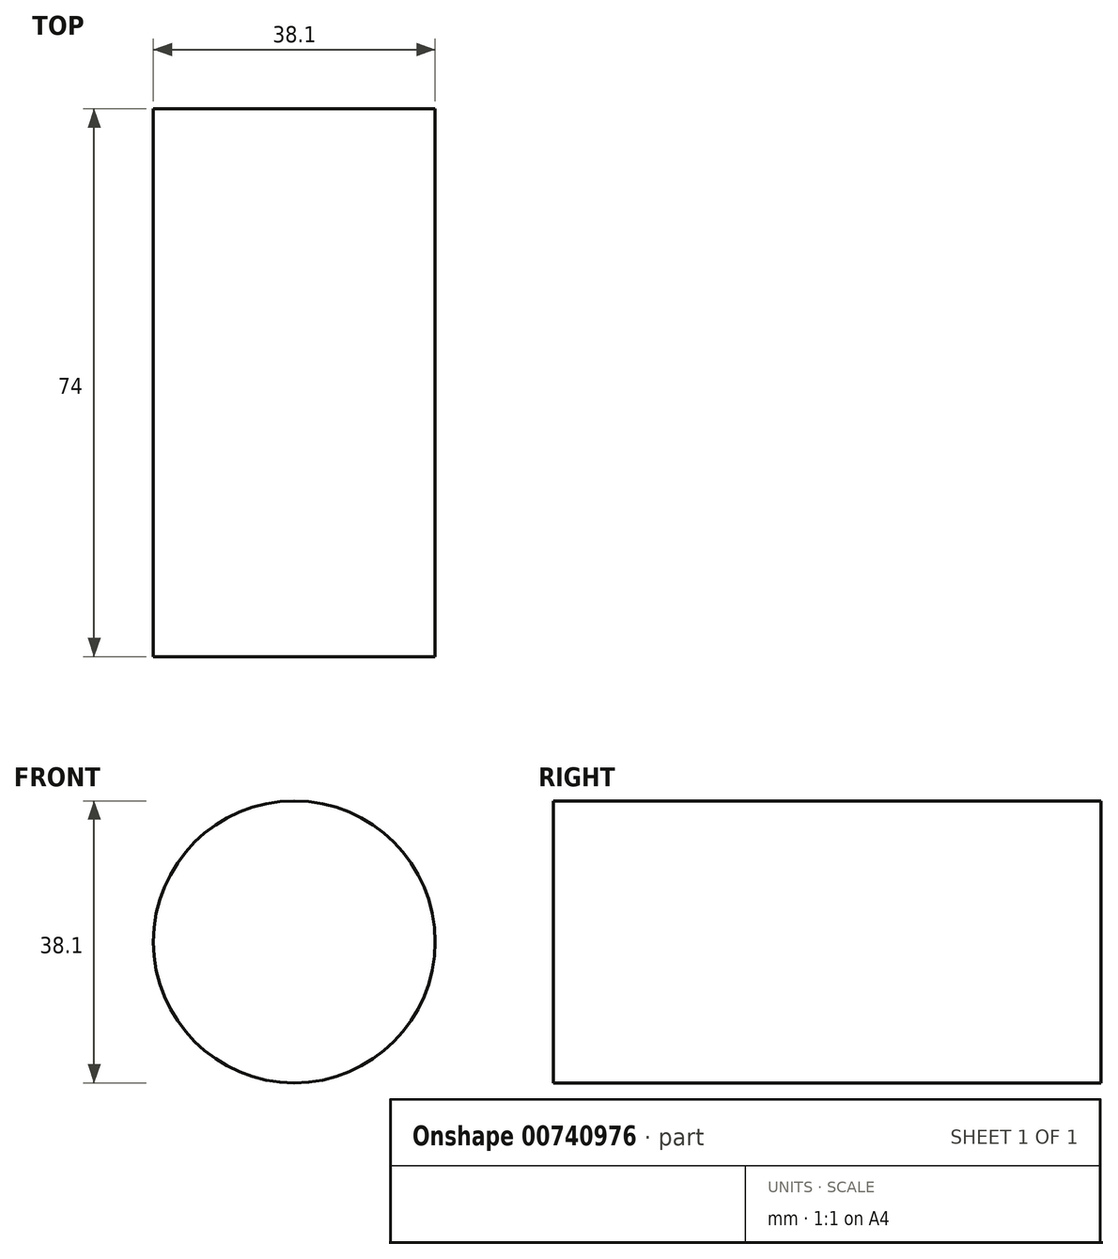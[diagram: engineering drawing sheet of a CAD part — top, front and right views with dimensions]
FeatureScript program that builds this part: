
annotation { "Feature Type Name" : "Feature", "Feature Type Description" : "" }
export const myFeature = defineFeature(function(context is Context, id is Id, definition is map)
    precondition{}
    {
        {
            var Q0;
            Q0=qCreatedBy(makeId("Front.planeOp"),FACE);
            var sketch = newSketch(context, id + "F0", { "sketchPlane" : qUnion([Q0])});
            skLineSegment(sketch, "E0", {"start": v(0, 0) * mm, "end": v(0, 907.18) * mm});
            skLineSegment(sketch, "E1.0", {"start": v(554, 0.09) * mm, "end": v(554, 907.18) * mm});
            skLineSegment(sketch, "E2.0", {"start": v(-554, 0) * mm, "end": v(-554, 907.18) * mm});
            skCircle(sketch, "E3", {"center": v(-554, 0) * mm, "radius": 330.2 * mm});
            skCircle(sketch, "E4", {"center": v(554, 0.09) * mm, "radius": 330.2 * mm});
            skLineSegment(sketch, "E5", {"start": v(554, 0.09) * mm, "end": v(195.65, 933.63) * mm});
            skLineSegment(sketch, "E6", {"start": v(554, 0.09) * mm, "end": v(-982.33, 0.09) * mm});
            skLineSegment(sketch, "E7.0", {"start": v(506.4, -18.22) * mm, "end": v(148.03, 915.36) * mm});
            skLineSegment(sketch, "E8", {"start": v(-554, 0) * mm, "end": v(-554, -234.33) * mm});
            skLineSegment(sketch, "E9.0", {"start": v(553.66, -62.91) * mm, "end": v(-982.33, -62.91) * mm});
            skLineSegment(sketch, "E10", {"start": v(-554, 0) * mm, "end": v(-118.52, -62.91) * mm});
            skCircle(sketch, "E11", {"center": v(-118.52, -62.91) * mm, "radius": 19.05 * mm});
            skLineSegment(sketch, "E12", {"start": v(-118.52, -62.91) * mm, "end": v(-241.22, 351.3) * mm});
            skLineSegment(sketch, "E13", {"start": v(554, 0.09) * mm, "end": v(647.36, 35.92) * mm});
            skLineSegment(sketch, "E14.0", {"start": v(380.9, 451) * mm, "end": v(474.27, 486.84) * mm});
            skLineSegment(sketch, "E15.0", {"start": v(553.66, 531.59) * mm, "end": v(-982.33, 531.59) * mm});
            skLineSegment(sketch, "E16", {"start": v(295.35, 531.59) * mm, "end": v(388.7, 567.42) * mm});
            skLineSegment(sketch, "E17", {"start": v(-118.52, -62.91) * mm, "end": v(-118.52, 697.77) * mm});
            skLineSegment(sketch, "E18", {"start": v(-576.5, 20.62) * mm, "end": v(-218.07, 273.16) * mm});
            skFitSpline(sketch, "E19", {"points": [v(302.01, 514.22) * mm, v(198.26, 465.6) * mm, v(-99.72, 282.84) * mm, v(-201.64, 217.7) * mm], "startDerivative": vector(-323.38, -130.8) * mm, "endDerivative": vector(-302.4, -193.44) * mm});
            skArc(sketch, "E20", {"start": v(-99.72, 282.84) * mm, "mid": v(-166.62, 269.88) * mm, "end": v(-226.65, 302.13) * mm});
            skFitSpline(sketch, "E21", {"points": [v(317.76, 473.2) * mm, v(251.9, 425.88) * mm, v(-104.17, -50.4) * mm], "startDerivative": vector(-211.28, -111.14) * mm, "endDerivative": vector(-574.72, -824.77) * mm});
            skSolve(sketch);
        }
        {
            var Q0;
            {var subQ0=sQuery(id+"F0.wireOp",EDGE,"E9.0");var subQ2=sQuery(id+"F0.wireOp",EDGE,"E11");var subQ3=makeQuery(id+"F0.imprint","INTERSECT",VERTEX,{"disambiguationData":[OD(0.0)],"derivedFrom":[subQ0,subQ2]});Q0=makeQuery(id+"F0.imprint","IMPRINT",FACE,{"disambiguationData":[TD([[makeQuery(id+"F0.imprint","IMPRINT",EDGE,{"disambiguationData":[TD([[subQ3,1.0]])],"derivedFrom":subQ2}),1.0]])]});}
            var Q1;
            {var subQ3=sQuery(id+"F0.wireOp",EDGE,"E11");var subQ5=makeQuery(id+"F0.imprint","INTERSECT",VERTEX,{"derivedFrom":[subQ3,sQuery(id+"F0.wireOp",EDGE,"E21")]});Q1=makeQuery(id+"F0.imprint","IMPRINT",FACE,{"disambiguationData":[TD([[makeQuery(id+"F0.imprint","IMPRINT",EDGE,{"disambiguationData":[TD([[subQ5,1.0]])],"derivedFrom":subQ3}),1.0]])]});}
            var Q2;
            {var subQ1=sQuery(id+"F0.wireOp",EDGE,"E10");var subQ3=sQuery(id+"F0.wireOp",EDGE,"E11");var subQ4=makeQuery(id+"F0.imprint","INTERSECT",VERTEX,{"derivedFrom":[subQ1,subQ3]});Q2=makeQuery(id+"F0.imprint","IMPRINT",FACE,{"disambiguationData":[TD([[makeQuery(id+"F0.imprint","IMPRINT",EDGE,{"disambiguationData":[TD([[subQ4,1.0]])],"derivedFrom":subQ3}),1.0]])]});}
            var Q3;
            {var subQ0=sQuery(id+"F0.wireOp",EDGE,"E17");var subQ1=sQuery(id+"F0.wireOp",EDGE,"E11");var subQ2=makeQuery(id+"F0.imprint","INTERSECT",VERTEX,{"derivedFrom":[subQ1,subQ0]});Q3=makeQuery(id+"F0.imprint","IMPRINT",FACE,{"disambiguationData":[TD([[makeQuery(id+"F0.imprint","IMPRINT",EDGE,{"disambiguationData":[TD([[subQ2,-1.0]])],"derivedFrom":subQ1}),1.0]])]});}
            var Q4;
            {var subQ1=sQuery(id+"F0.wireOp",EDGE,"E9.0");var subQ3=sQuery(id+"F0.wireOp",EDGE,"E11");var subQ4=makeQuery(id+"F0.imprint","INTERSECT",VERTEX,{"disambiguationData":[OD(1.0)],"derivedFrom":[subQ1,subQ3]});Q4=makeQuery(id+"F0.imprint","IMPRINT",FACE,{"disambiguationData":[TD([[makeQuery(id+"F0.imprint","IMPRINT",EDGE,{"disambiguationData":[TD([[subQ4,1.0]])],"derivedFrom":subQ3}),1.0]])]});}
            var Q5;
            Q5=sQuery(id+"F0.wireOp",EDGE,"E11");
            extrude(context, id + "F1", {"entities" : qUnion([Q0, Q1, Q2, Q3, Q4]), "surfaceEntities" : qUnion([Q5]), "endBound" : BoundingType.SYMMETRIC, "depth" : 74 * mm, "offsetDistance" : 25 * mm});
        }
    });
